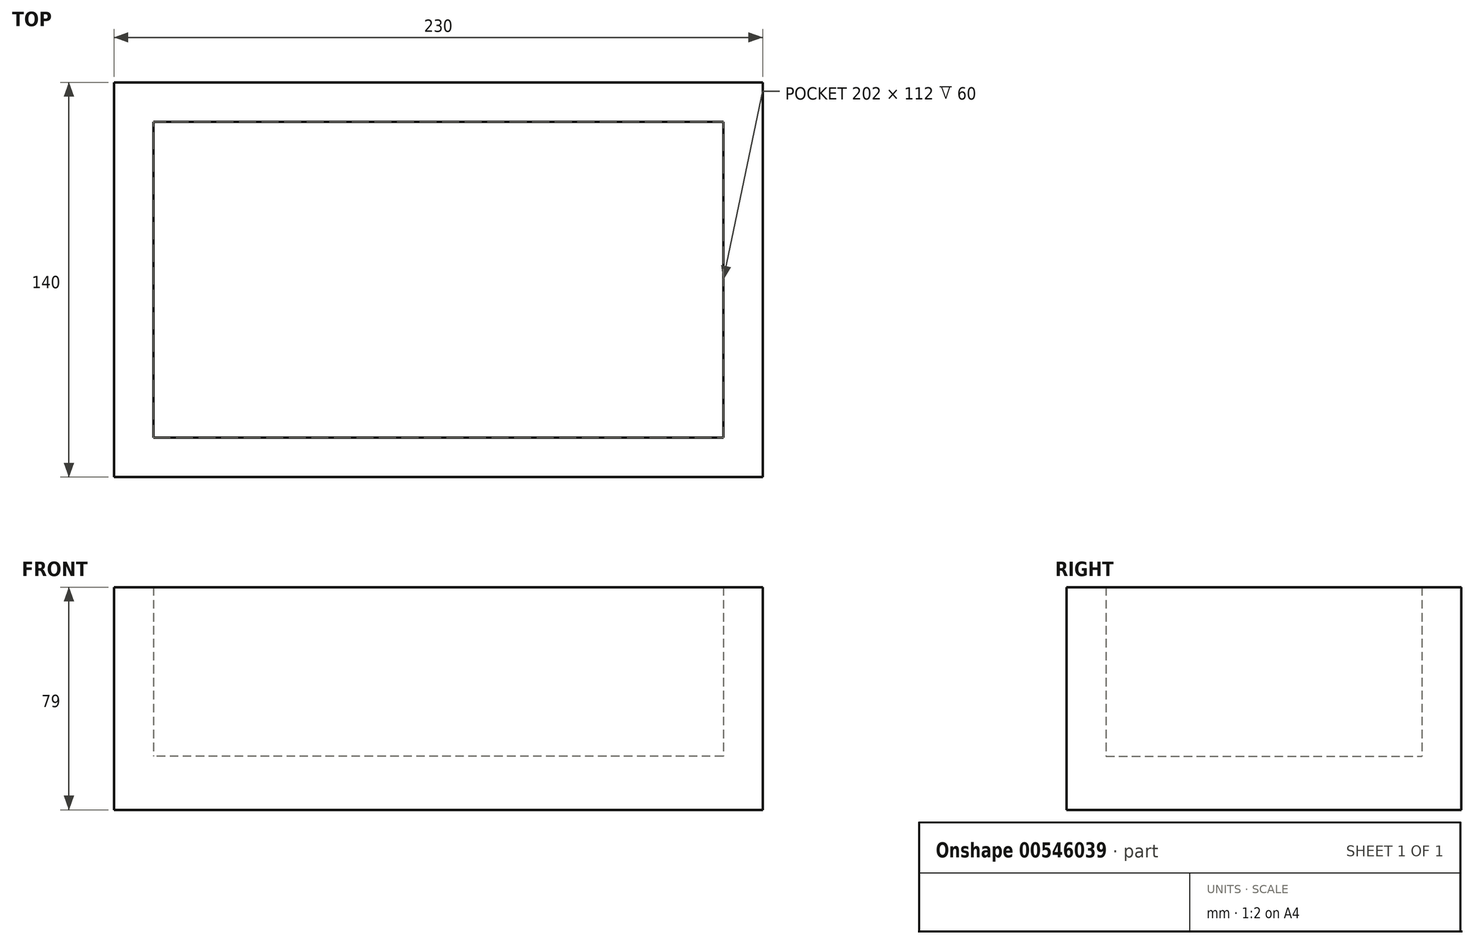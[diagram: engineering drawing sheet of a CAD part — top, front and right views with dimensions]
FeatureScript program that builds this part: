
annotation { "Feature Type Name" : "Feature", "Feature Type Description" : "" }
export const myFeature = defineFeature(function(context is Context, id is Id, definition is map)
    precondition{}
    {
        {
            var Q0;
            Q0=qCreatedBy(makeId("Top.planeOp"),FACE);
            var sketch = newSketch(context, id + "F0", { "sketchPlane" : qUnion([Q0])});
            skLineSegment(sketch, "E0.bottom", {"start": v(115, -70) * mm, "end": v(-115, -70) * mm});
            skLineSegment(sketch, "E0.top", {"start": v(115, 70) * mm, "end": v(-115, 70) * mm});
            skLineSegment(sketch, "E0.left", {"start": v(115, -70) * mm, "end": v(115, 70) * mm});
            skLineSegment(sketch, "E0.right", {"start": v(-115, -70) * mm, "end": v(-115, 70) * mm});
            skPoint(sketch, "E0.middle", {"position": v(0, 0) * mm});
            skSolve(sketch);
        }
        {
            var Q0;
            Q0 = qSketchRegion(id + "F0", true);
            extrude(context, id + "F1", {"entities" : qUnion([Q0]), "depth" : 19 * mm, "offsetDistance" : 25 * mm});
        }
        {
            var Q0;
            Q0=makeQuery(id+"F1.opExtrude","CAP_FACE",FACE,{"disambiguationData":[OSD([sQuery(id+"F0.wireOp",EDGE,"E0.bottom"),sQuery(id+"F0.wireOp",EDGE,"E0.top"),sQuery(id+"F0.wireOp",EDGE,"E0.left"),sQuery(id+"F0.wireOp",EDGE,"E0.right")])],"isStart":false});
            var sketch = newSketch(context, id + "F2", { "sketchPlane" : qUnion([Q0])});
            skLineSegment(sketch, "E1.bottom", {"start": v(101, -56) * mm, "end": v(-101, -56) * mm});
            skLineSegment(sketch, "E1.top", {"start": v(101, 56) * mm, "end": v(-101, 56) * mm});
            skLineSegment(sketch, "E1.left", {"start": v(101, -56) * mm, "end": v(101, 56) * mm});
            skLineSegment(sketch, "E1.right", {"start": v(-101, -56) * mm, "end": v(-101, 56) * mm});
            skPoint(sketch, "E1.middle", {"position": v(0, 0) * mm});
            skSolve(sketch);
        }
        {
            var Q0;
            Q0=makeQuery(id+"F2.imprint","IMPRINT",FACE,{"disambiguationData":[TD([[makeQuery(id+"F2.imprint","IMPRINT",EDGE,{"derivedFrom":sQuery(id+"F2.wireOp",EDGE,"E1.bottom")}),1.0]])]});
            extrude(context, id + "F3", {"entities" : qUnion([Q0]), "operationType" : NewBodyOperationType.ADD, "depth" : 60 * mm, "offsetDistance" : 25 * mm});
        }
    });
